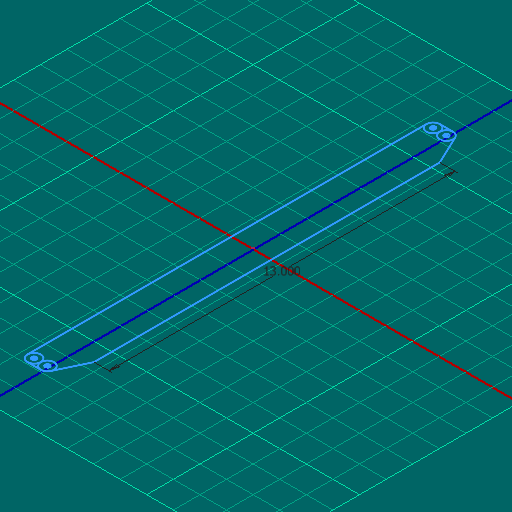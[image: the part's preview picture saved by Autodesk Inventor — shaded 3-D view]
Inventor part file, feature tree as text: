
AUTODESK INVENTOR PART (.ipt)
format: ipt  version: 2025 (Build 290162000, 162)  size: 105,984 bytes
history: native  units: in
note: dims shown in document units (in); Inventor stores cm internally (conversion verified against a paired STEP export)
features: sketch x1
ambient origin geometry x8: Origin, YZ Plane, XZ Plane, XY Plane, X Axis, Y Axis, Z Axis, Center Point
feature tree (1):
  sketch  "Sketch1"  dims[d0=13.0in]
